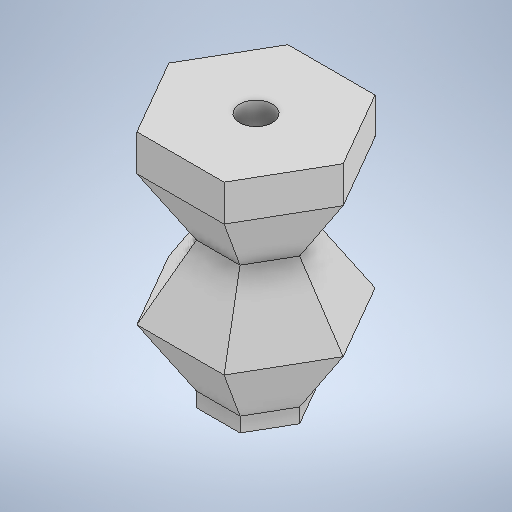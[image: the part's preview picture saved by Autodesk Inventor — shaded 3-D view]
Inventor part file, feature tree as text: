
AUTODESK INVENTOR PART (.ipt)
format: ipt  version: 2025.1 (Build 291241000, 241)  size: 296,448 bytes
history: native  units: mm
features: sketch x5, other x3, extrude x3, mirror x2, projected_geometry x2, loft x1, shell x1
ambient origin geometry x8: Origin, YZ Plane, XZ Plane, XY Plane, X Axis, Y Axis, Z Axis, Center Point
bodies: Body1 (feature_tree)
feature tree (17):
  other  "솔리드1"
  sketch  "스케치1"
  other  "작업 평면1"
  loft  "로프트1"
  mirror  "미러1"
  other  "작업 평면2"
  mirror  "미러2"
  shell  "쉘1"  Thickness=9.0mm
  extrude  "돌출1"  Depth=12.0mm
  extrude  "돌출2"  TaperAngle=0.0deg  [1 undecoded]
  extrude  "돌출3"  TaperAngle=0.0deg  [1 undecoded]
  sketch  "스케치2"
  sketch  "스케치3"
  projected_geometry  "투영된 루프1"
  sketch  "스케치4"
  projected_geometry  "투영된 루프2"
  sketch  "스케치5"
note: 2 required parameter values undecoded (feature->parameter linkage not recoverable at this tier; creation-order binding heuristic only, values carry confidence <= 0.55)
